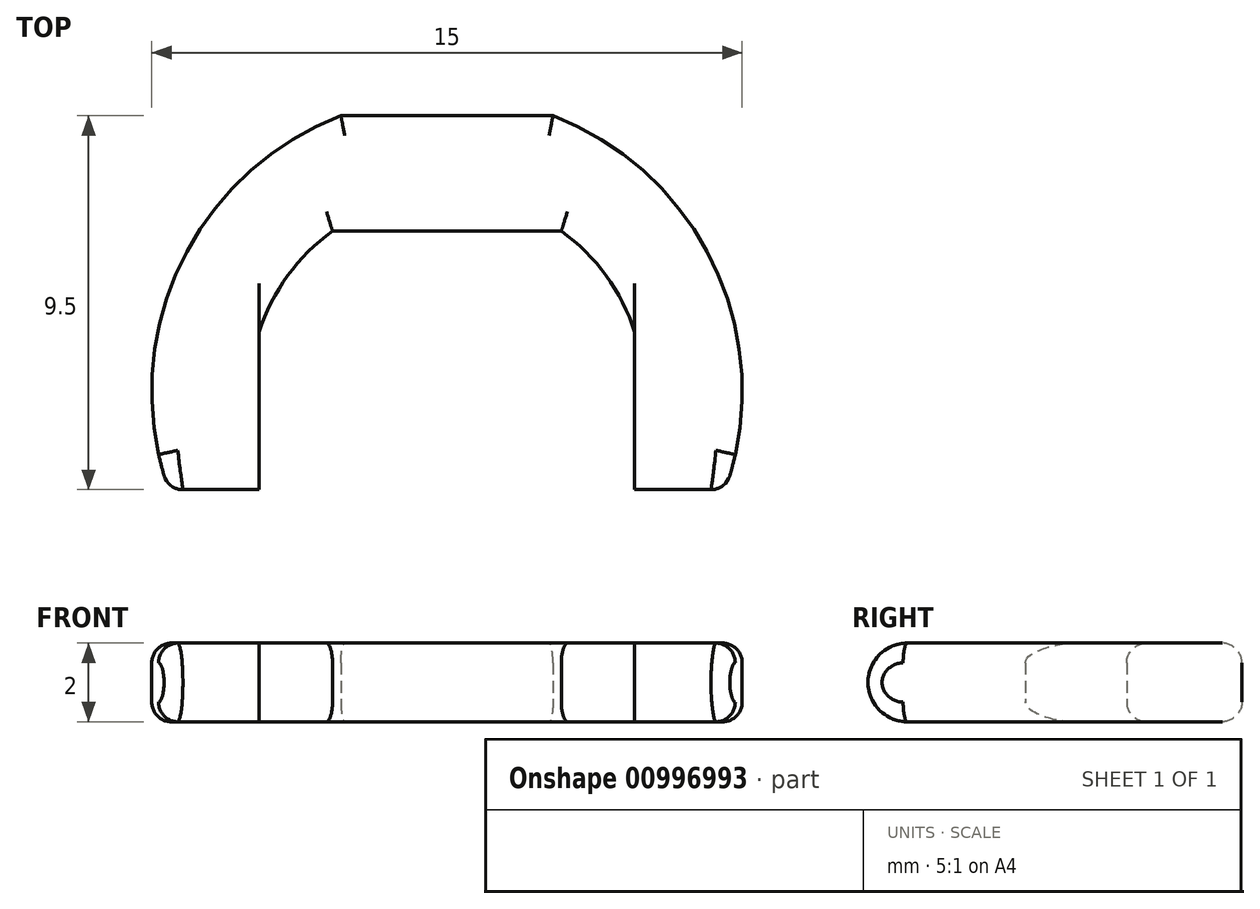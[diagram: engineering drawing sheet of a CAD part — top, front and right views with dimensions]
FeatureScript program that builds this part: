
annotation { "Feature Type Name" : "Feature", "Feature Type Description" : "" }
export const myFeature = defineFeature(function(context is Context, id is Id, definition is map)
    precondition{}
    {
        {
            var Q0;
            Q0=qCreatedBy(makeId("Top.planeOp"),FACE);
            var sketch = newSketch(context, id + "F0", { "sketchPlane" : qUnion([Q0])});
            skCircle(sketch, "E0", {"center": v(0, 0) * mm, "radius": 7.5 * mm});
            skLineSegment(sketch, "E1", {"start": v(-2.7, 7) * mm, "end": v(2.7, 7) * mm});
            skCircle(sketch, "E2", {"center": v(0, 0) * mm, "radius": 5 * mm});
            skLineSegment(sketch, "E3", {"start": v(-2.9, 4.07) * mm, "end": v(2.9, 4.07) * mm});
            skCircle(sketch, "E4", {"center": v(0, 0) * mm, "radius": 1.5 * mm});
            skLineSegment(sketch, "E5", {"start": v(-4.77, 1.5) * mm, "end": v(4.77, 1.5) * mm});
            skLineSegment(sketch, "E6", {"start": v(-7.07, -2.5) * mm, "end": v(7.07, -2.5) * mm});
            skLineSegment(sketch, "E7", {"start": v(-4.77, 1.5) * mm, "end": v(-4.77, -2.5) * mm});
            skLineSegment(sketch, "E8", {"start": v(4.77, 1.5) * mm, "end": v(4.77, -2.5) * mm});
            skSolve(sketch);
        }
        {
            var Q0;
            {var subQ17=sQuery(id+"F0.wireOp",EDGE,"E1");Q0=makeQuery(id+"F0.imprint","IMPRINT",FACE,{"disambiguationData":[TD([[makeQuery(id+"F0.imprint","IMPRINT",EDGE,{"derivedFrom":subQ17}),-1.0]])]});}
            var Q1;
            {var subQ0=sQuery(id+"F0.wireOp",EDGE,"E3");Q1=makeQuery(id+"F0.imprint","IMPRINT",FACE,{"disambiguationData":[TD([[makeQuery(id+"F0.imprint","IMPRINT",EDGE,{"derivedFrom":subQ0}),1.0]])]});}
            var Q2;
            {var subQ0=sQuery(id+"F0.wireOp",EDGE,"E7");var subQ1=sQuery(id+"F0.wireOp",EDGE,"E2");var subQ3=makeQuery(id+"F0.imprint","INTERSECT",VERTEX,{"derivedFrom":[subQ1,subQ0]});Q2=makeQuery(id+"F0.imprint","IMPRINT",FACE,{"disambiguationData":[TD([[makeQuery(id+"F0.imprint","IMPRINT",EDGE,{"disambiguationData":[TD([[subQ3,1.0]])],"derivedFrom":subQ1}),1.0]])]});}
            var Q3;
            {var subQ0=sQuery(id+"F0.wireOp",EDGE,"E8");var subQ1=sQuery(id+"F0.wireOp",EDGE,"E2");var subQ3=makeQuery(id+"F0.imprint","INTERSECT",VERTEX,{"derivedFrom":[subQ1,subQ0]});Q3=makeQuery(id+"F0.imprint","IMPRINT",FACE,{"disambiguationData":[TD([[makeQuery(id+"F0.imprint","IMPRINT",EDGE,{"disambiguationData":[TD([[subQ3,-1.0]])],"derivedFrom":subQ1}),1.0]])]});}
            extrude(context, id + "F1", {"entities" : qUnion([Q0, Q1, Q2, Q3]), "depth" : 2 * mm, "offsetDistance" : 25 * mm});
        }
        {
            var Q0;
            {var subQ0=sQuery(id+"F0.wireOp",EDGE,"E6");Q0=makeQuery(id+"F1.opExtrude","CAP_EDGE",EDGE,{"disambiguationData":[OSD([subQ0]),TDD([makeQuery(id+"F0.imprint","IMPRINT",EDGE,{"disambiguationData":[TD([[makeQuery(id+"F0.imprint","INTERSECT",VERTEX,{"disambiguationData":[OD(1.0)],"derivedFrom":[sQuery(id+"F0.wireOp",EDGE,"E0"),subQ0]}),1.0]])],"derivedFrom":subQ0})])],"isStart":false});}
            var Q1;
            {var subQ0=sQuery(id+"F0.wireOp",EDGE,"E6");Q1=makeQuery(id+"F1.opExtrude","CAP_EDGE",EDGE,{"disambiguationData":[OSD([subQ0]),TDD([makeQuery(id+"F0.imprint","IMPRINT",EDGE,{"disambiguationData":[TD([[makeQuery(id+"F0.imprint","INTERSECT",VERTEX,{"disambiguationData":[OD(0.0)],"derivedFrom":[sQuery(id+"F0.wireOp",EDGE,"E0"),subQ0]}),-1.0]])],"derivedFrom":subQ0})])],"isStart":false});}
            var Q2;
            {var subQ0=sQuery(id+"F0.wireOp",EDGE,"E6");Q2=makeQuery(id+"F1.opExtrude","CAP_EDGE",EDGE,{"disambiguationData":[OSD([subQ0]),TDD([makeQuery(id+"F0.imprint","IMPRINT",EDGE,{"disambiguationData":[TD([[makeQuery(id+"F0.imprint","INTERSECT",VERTEX,{"disambiguationData":[OD(1.0)],"derivedFrom":[sQuery(id+"F0.wireOp",EDGE,"E0"),subQ0]}),1.0]])],"derivedFrom":subQ0})])],"isStart":true});}
            var Q3;
            {var subQ0=sQuery(id+"F0.wireOp",EDGE,"E6");Q3=makeQuery(id+"F1.opExtrude","CAP_EDGE",EDGE,{"disambiguationData":[OSD([subQ0]),TDD([makeQuery(id+"F0.imprint","IMPRINT",EDGE,{"disambiguationData":[TD([[makeQuery(id+"F0.imprint","INTERSECT",VERTEX,{"disambiguationData":[OD(0.0)],"derivedFrom":[sQuery(id+"F0.wireOp",EDGE,"E0"),subQ0]}),-1.0]])],"derivedFrom":subQ0})])],"isStart":true});}
            fillet(context, id + "F2", {"entities" : qUnion([Q0, Q1, Q2, Q3]), "radius" : 1 * mm, "tangentPropagation" : true, "allowEdgeOverflow" : false});
        }
        {
            var Q0;
            {var subQ0=sQuery(id+"F0.wireOp",EDGE,"E0");Q0=makeQuery(id+"F1.opExtrude","CAP_EDGE",EDGE,{"disambiguationData":[OSD([subQ0]),TDD([makeQuery(id+"F0.imprint","IMPRINT",EDGE,{"disambiguationData":[TD([[makeQuery(id+"F0.imprint","INTERSECT",VERTEX,{"disambiguationData":[OD(1.0)],"derivedFrom":[subQ0,sQuery(id+"F0.wireOp",EDGE,"E1")]}),1.0]])],"derivedFrom":subQ0})])],"isStart":false});}
            var Q1;
            Q1=makeQuery(id+"F1.opExtrude","CAP_EDGE",EDGE,{"disambiguationData":[OSD([sQuery(id+"F0.wireOp",EDGE,"E1")])],"isStart":false});
            var Q2;
            {var subQ0=sQuery(id+"F0.wireOp",EDGE,"E0");Q2=makeQuery(id+"F1.opExtrude","CAP_EDGE",EDGE,{"disambiguationData":[OSD([subQ0]),TDD([makeQuery(id+"F0.imprint","IMPRINT",EDGE,{"disambiguationData":[TD([[makeQuery(id+"F0.imprint","INTERSECT",VERTEX,{"disambiguationData":[OD(0.0)],"derivedFrom":[subQ0,sQuery(id+"F0.wireOp",EDGE,"E1")]}),-1.0]])],"derivedFrom":subQ0})])],"isStart":false});}
            var Q3;
            Q3=makeQuery(id+"F1.opExtrude","CAP_EDGE",EDGE,{"disambiguationData":[OSD([sQuery(id+"F0.wireOp",EDGE,"E1")])],"isStart":true});
            var Q4;
            {var subQ0=sQuery(id+"F0.wireOp",EDGE,"E2");Q4=makeQuery(id+"F1.opExtrude","CAP_EDGE",EDGE,{"disambiguationData":[OSD([subQ0]),TDD([makeQuery(id+"F0.imprint","IMPRINT",EDGE,{"disambiguationData":[TD([[makeQuery(id+"F0.imprint","INTERSECT",VERTEX,{"disambiguationData":[OD(1.0)],"derivedFrom":[subQ0,sQuery(id+"F0.wireOp",EDGE,"E3")]}),1.0]])],"derivedFrom":subQ0})])],"isStart":false});}
            var Q5;
            Q5=makeQuery(id+"F1.opExtrude","CAP_EDGE",EDGE,{"disambiguationData":[OSD([sQuery(id+"F0.wireOp",EDGE,"E3")])],"isStart":false});
            var Q6;
            {var subQ0=sQuery(id+"F0.wireOp",EDGE,"E2");Q6=makeQuery(id+"F1.opExtrude","CAP_EDGE",EDGE,{"disambiguationData":[OSD([subQ0]),TDD([makeQuery(id+"F0.imprint","IMPRINT",EDGE,{"disambiguationData":[TD([[makeQuery(id+"F0.imprint","INTERSECT",VERTEX,{"disambiguationData":[OD(0.0)],"derivedFrom":[subQ0,sQuery(id+"F0.wireOp",EDGE,"E3")]}),-1.0]])],"derivedFrom":subQ0})])],"isStart":false});}
            var Q7;
            Q7=makeQuery(id+"F1.opExtrude","CAP_EDGE",EDGE,{"disambiguationData":[OSD([sQuery(id+"F0.wireOp",EDGE,"E3")])],"isStart":true});
            var Q8;
            {var subQ0=sQuery(id+"F0.wireOp",EDGE,"E2");Q8=makeQuery(id+"F1.opExtrude","CAP_EDGE",EDGE,{"disambiguationData":[OSD([subQ0]),TDD([makeQuery(id+"F0.imprint","IMPRINT",EDGE,{"disambiguationData":[TD([[makeQuery(id+"F0.imprint","INTERSECT",VERTEX,{"disambiguationData":[OD(1.0)],"derivedFrom":[subQ0,sQuery(id+"F0.wireOp",EDGE,"E3")]}),1.0]])],"derivedFrom":subQ0})])],"isStart":true});}
            var Q9;
            {var subQ0=sQuery(id+"F0.wireOp",EDGE,"E2");Q9=makeQuery(id+"F1.opExtrude","CAP_EDGE",EDGE,{"disambiguationData":[OSD([subQ0]),TDD([makeQuery(id+"F0.imprint","IMPRINT",EDGE,{"disambiguationData":[TD([[makeQuery(id+"F0.imprint","INTERSECT",VERTEX,{"disambiguationData":[OD(0.0)],"derivedFrom":[subQ0,sQuery(id+"F0.wireOp",EDGE,"E3")]}),-1.0]])],"derivedFrom":subQ0})])],"isStart":true});}
            fillet(context, id + "F3", {"entities" : qUnion([Q0, Q1, Q2, Q3, Q4, Q5, Q6, Q7, Q8, Q9]), "radius" : 0.5 * mm, "tangentPropagation" : true, "allowEdgeOverflow" : false});
        }
    });
